# Revit family: QF_Stero_SC-24-STEAM_L-R_cat
name_source: partatom
category: Specialty Equipment
revit_build: Autodesk Revit 2017 (Build: 20190508_0315(x64)
units: mm (PartAtom-declared; Revit-internal decimal feet)

## family parameters
Always vertical = Yes
Cut with Voids When Loaded = No
OmniClass Number = 23.40.40.14.31
OmniClass Title = Cleaning and Disposal Equipment
Part Type = Normal
Room Calculation Point = No
Round Connector Dimension = Use Diameter
Shared = No
Work Plane-Based = No

## types (3) — shared parameters
Accent Material = QF_Plastic-Black
Apparent Power = 3 kW
Assembly Code = E1090320
Booster Condensate Return Connection Height = 6 1/2"
Booster Condensate Return Size = 1/2"
Booster Hot Water Connection Height = 11 1/2"
Booster Hot Water Consumption = 0 GPM
Booster Hot Water Flow = 0 GPM
Booster Hot Water Maximum Pressure = 40.00 psi
Booster Hot Water Minimum Pressure = 20.00 psi
Booster Hot Water Size = 3/4"
Booster Hot Water Temperature = 140 °F
Booster Plumbing Connection Type = NPT
Booster Steam Pounds per Hour = 150
Booster Steam Supply Connection Height = 23"
Booster Steam Supply Maximum Pressure = 40.00 psi
Booster Steam Supply Minimum Pressure = 15.00 psi
Booster Steam Supply Size = 3/4"
Booster Steam Supply Volume = 0 GPM
CSI MasterFormat = 11 48 13
Clearance Material = QF_Finishes_Clearances
Cold Water Connection Height = 59 5/8"
Cold Water Maximum Pressure = 40.00 psi
Cold Water Minimum Pressure = 20.00 psi
Cold Water Size = 3/4"
Conveyor Motor HP = 1/4
Curtain Material = QF_Plastic-Cyan
Cycle = 60 Hz
Depth = 40"
Description = DISHWASHING MACHINE
Elec Conn Connection Height = 68 1/2"
Elec Conn RI Height = 0"
Exhaust Vent Depth = 24 7/8"
Exhaust Vent Width = 3 7/8"
Exhaust Volume-Load End = 200 CFM
Exhaust Volume-Unload End = 400 CFM
Foodservice Equipment Identifier = Yes
Handle Material = QF_Plastic-Blue
Height = 71 1/2"
Indirect Waste Connection Height = 8 1/2"
Indirect Waste Size = 2"
Manufacturer = STERO
Material = QF_Metal-Stainless-Satin
Max Overcurrent Protection = 15 A
Min Ckt Ampacity = 0 A
Model = SC-24 STEAM
Number of Poles = 3
Phase = 3
URL = WWW.STERO.COM
Wash Motor HP = 2
Width = 98"

## per-type parameters (varying)
| type | FL Amps | Volts |
| SC-24_208/60/3 | 8 A | 208 V |
| SC-24_240/60/3 | 7 A | 240 V |
| SC-24_480/60/3 | 4 A | 480 V |

## geometry (parser evidence)
native form markers: Sweep x5
no freeform markers — native parametric forms only
